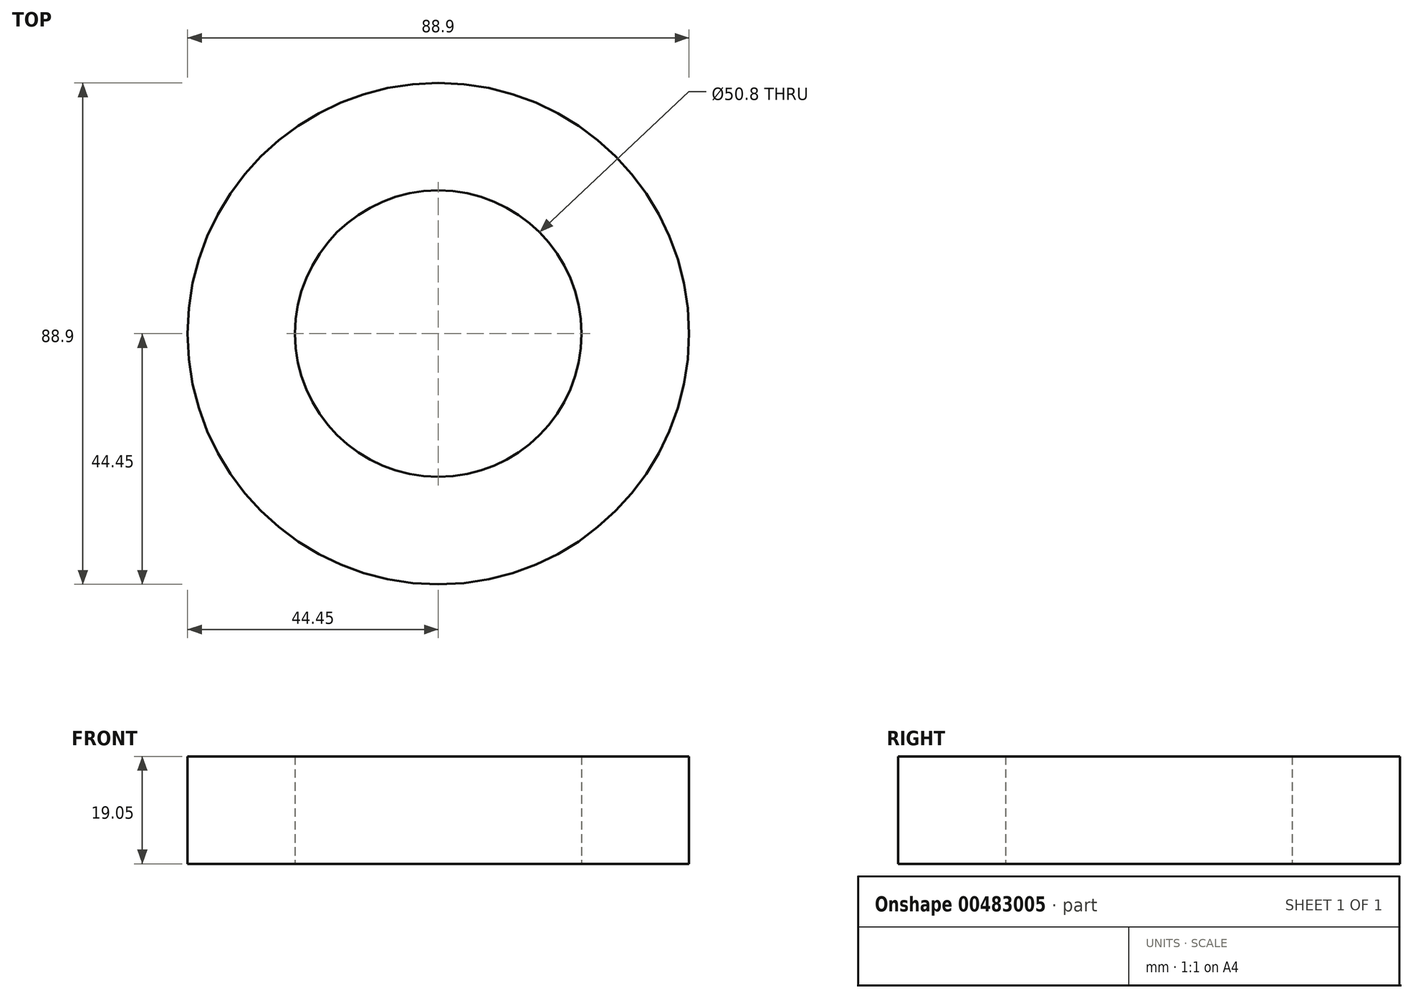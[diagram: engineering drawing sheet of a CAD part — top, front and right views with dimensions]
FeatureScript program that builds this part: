
annotation { "Feature Type Name" : "Feature", "Feature Type Description" : "" }
export const myFeature = defineFeature(function(context is Context, id is Id, definition is map)
    precondition{}
    {
        {
            var Q0;
            Q0=qCreatedBy(makeId("Top.planeOp"),FACE);
            var sketch = newSketch(context, id + "F0", { "sketchPlane" : qUnion([Q0])});
            skCircle(sketch, "E0", {"center": v(0, 0) * mm, "radius": 44.45 * mm});
            skCircle(sketch, "E1", {"center": v(0, 0) * mm, "radius": 25.4 * mm});
            skCircle(sketch, "E2.cCircle", {"center": v(0, 0) * mm, "radius": 15.88 * mm, "construction": true});
            skLineSegment(sketch, "E2.0", {"start": v(15.88, 27.5) * mm, "end": v(15.88, -27.5) * mm, "construction": true});
            skLineSegment(sketch, "E2.1", {"start": v(15.88, -27.5) * mm, "end": v(-31.75, 0) * mm, "construction": true});
            skLineSegment(sketch, "E2.2", {"start": v(-31.75, 0) * mm, "end": v(15.88, 27.5) * mm, "construction": true});
            skPoint(sketch, "E2.0.midPoint", {"position": v(15.88, 0) * mm});
            skSolve(sketch);
        }
        {
            var Q0;
            Q0=makeQuery(id+"F0.imprint","IMPRINT",FACE,{"disambiguationData":[TD([[makeQuery(id+"F0.imprint","IMPRINT",EDGE,{"derivedFrom":sQuery(id+"F0.wireOp",EDGE,"E0")}),1.0]])]});
            extrude(context, id + "F1", {"entities" : qUnion([Q0]), "depth" : 19.05 * mm});
        }
    });
